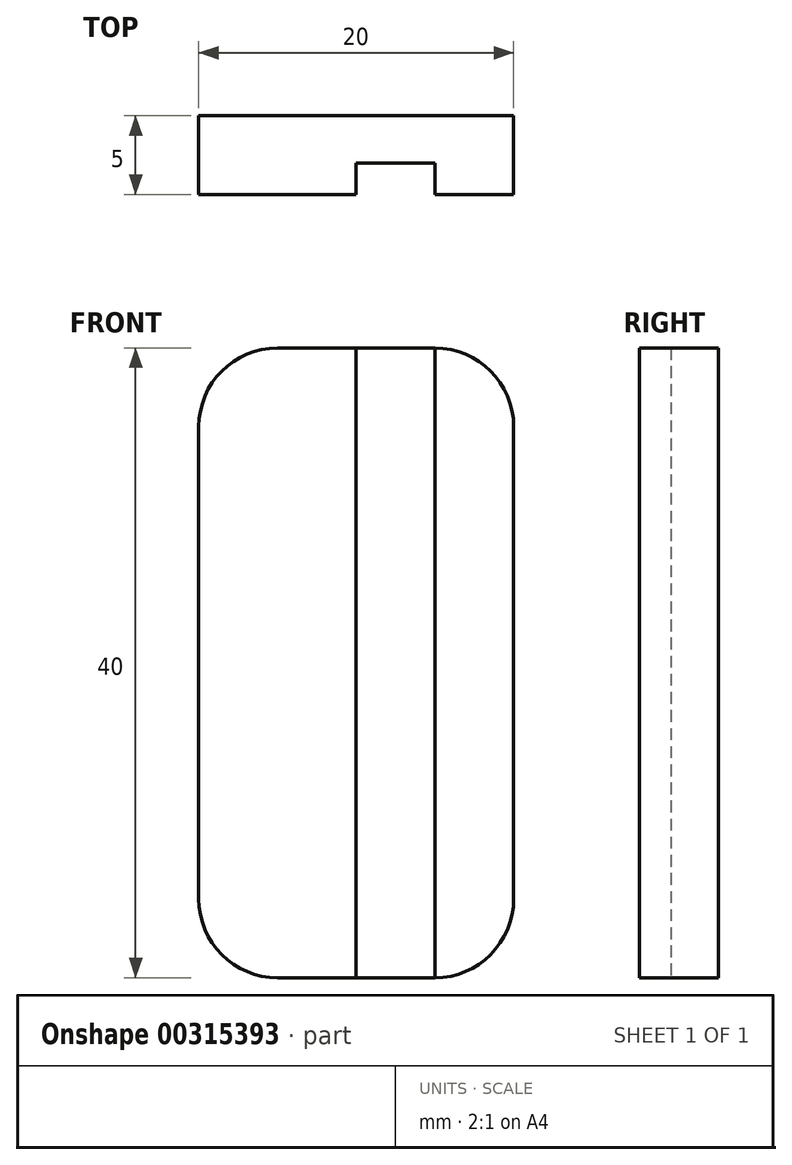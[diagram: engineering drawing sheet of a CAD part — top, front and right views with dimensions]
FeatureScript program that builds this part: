
annotation { "Feature Type Name" : "Feature", "Feature Type Description" : "" }
export const myFeature = defineFeature(function(context is Context, id is Id, definition is map)
    precondition{}
    {
        {
            var Q0;
            Q0=qCreatedBy(makeId("Front.planeOp"),FACE);
            var sketch = newSketch(context, id + "F0", { "sketchPlane" : qUnion([Q0])});
            skLineSegment(sketch, "E0.bottom", {"start": v(-10, 20) * mm, "end": v(10, 20) * mm});
            skLineSegment(sketch, "E0.top", {"start": v(-10, -20) * mm, "end": v(10, -20) * mm});
            skLineSegment(sketch, "E0.left", {"start": v(-10, 20) * mm, "end": v(-10, -20) * mm});
            skLineSegment(sketch, "E0.right", {"start": v(10, 20) * mm, "end": v(10, -20) * mm});
            skPoint(sketch, "E0.middle", {"position": v(0, 0) * mm});
            skSolve(sketch);
        }
        {
            var Q0;
            Q0=makeQuery(id+"F0.imprint","IMPRINT",FACE,{"disambiguationData":[TD([[makeQuery(id+"F0.imprint","IMPRINT",EDGE,{"derivedFrom":sQuery(id+"F0.wireOp",EDGE,"E0.bottom")}),-1.0]])]});
            extrude(context, id + "F1", {"entities" : qUnion([Q0]), "depth" : 5 * mm});
        }
        {
            var Q0;
            Q0=makeQuery(id+"F1.opExtrude","SWEPT_FACE",FACE,{"disambiguationData":[OSD([sQuery(id+"F0.wireOp",EDGE,"E0.top")])]});
            var sketch = newSketch(context, id + "F2", { "sketchPlane" : qUnion([Q0])});
            skLineSegment(sketch, "E1.0.0", {"start": v(-10, 0) * mm, "end": v(10, 0) * mm});
            skLineSegment(sketch, "E1.0.1", {"start": v(10, 0) * mm, "end": v(10, 5) * mm});
            skLineSegment(sketch, "E1.0.2", {"start": v(10, 5) * mm, "end": v(-10, 5) * mm});
            skLineSegment(sketch, "E1.0.3", {"start": v(-10, 5) * mm, "end": v(-10, 0) * mm});
            skLineSegment(sketch, "E2", {"start": v(0, 5) * mm, "end": v(0, 0) * mm, "construction": true});
            skLineSegment(sketch, "E3.bottom", {"start": v(0, 5) * mm, "end": v(-5, 5) * mm});
            skLineSegment(sketch, "E3.top", {"start": v(0, 3) * mm, "end": v(-5, 3) * mm});
            skLineSegment(sketch, "E3.left", {"start": v(0, 5) * mm, "end": v(0, 3) * mm});
            skLineSegment(sketch, "E3.right", {"start": v(-5, 5) * mm, "end": v(-5, 3) * mm});
            skLineSegment(sketch, "E4.MirrorCS", {"start": v(0, 3) * mm, "end": v(5, 3) * mm});
            skLineSegment(sketch, "E5.MirrorCS", {"start": v(5, 5) * mm, "end": v(5, 3) * mm});
            skSolve(sketch);
        }
        {
            var Q0;
            Q0=makeQuery(id+"F2.imprint","IMPRINT",FACE,{"disambiguationData":[TD([[makeQuery(id+"F2.imprint","IMPRINT",EDGE,{"derivedFrom":sQuery(id+"F2.wireOp",EDGE,"E3.bottom")}),-1.0]])]});
            var Q1;
            {var subQ0=sQuery(id+"F2.wireOp",EDGE,"E3.left");Q1=makeQuery(id+"F2.imprint","IMPRINT",FACE,{"disambiguationData":[TD([[makeQuery(id+"F2.imprint","IMPRINT",EDGE,{"derivedFrom":subQ0}),1.0]])]});}
            extrude(context, id + "F3", {"entities" : qUnion([Q0, Q1]), "operationType" : NewBodyOperationType.REMOVE, "endBound" : BoundingType.THROUGH_ALL, "oppositeDirection" : true, "depth" : 25 * mm});
        }
        {
            var Q0;
            Q0=makeQuery(id+"F1.opExtrude","SWEPT_EDGE",EDGE,{"disambiguationData":[OSD([sQuery(id+"F0.wireOp",EDGE,"E0.top"),sQuery(id+"F0.wireOp",EDGE,"E0.left")])]});
            var Q1;
            Q1=makeQuery(id+"F1.opExtrude","SWEPT_EDGE",EDGE,{"disambiguationData":[OSD([sQuery(id+"F0.wireOp",EDGE,"E0.top"),sQuery(id+"F0.wireOp",EDGE,"E0.right")])]});
            var Q2;
            Q2=makeQuery(id+"F1.opExtrude","SWEPT_EDGE",EDGE,{"disambiguationData":[OSD([sQuery(id+"F0.wireOp",EDGE,"E0.bottom"),sQuery(id+"F0.wireOp",EDGE,"E0.left")])]});
            var Q3;
            Q3=makeQuery(id+"F1.opExtrude","SWEPT_EDGE",EDGE,{"disambiguationData":[OSD([sQuery(id+"F0.wireOp",EDGE,"E0.bottom"),sQuery(id+"F0.wireOp",EDGE,"E0.right")])]});
            fillet(context, id + "F4", {"entities" : qUnion([Q0, Q1, Q2, Q3]), "radius" : 5 * mm, "tangentPropagation" : true, "allowEdgeOverflow" : false});
        }
    });
